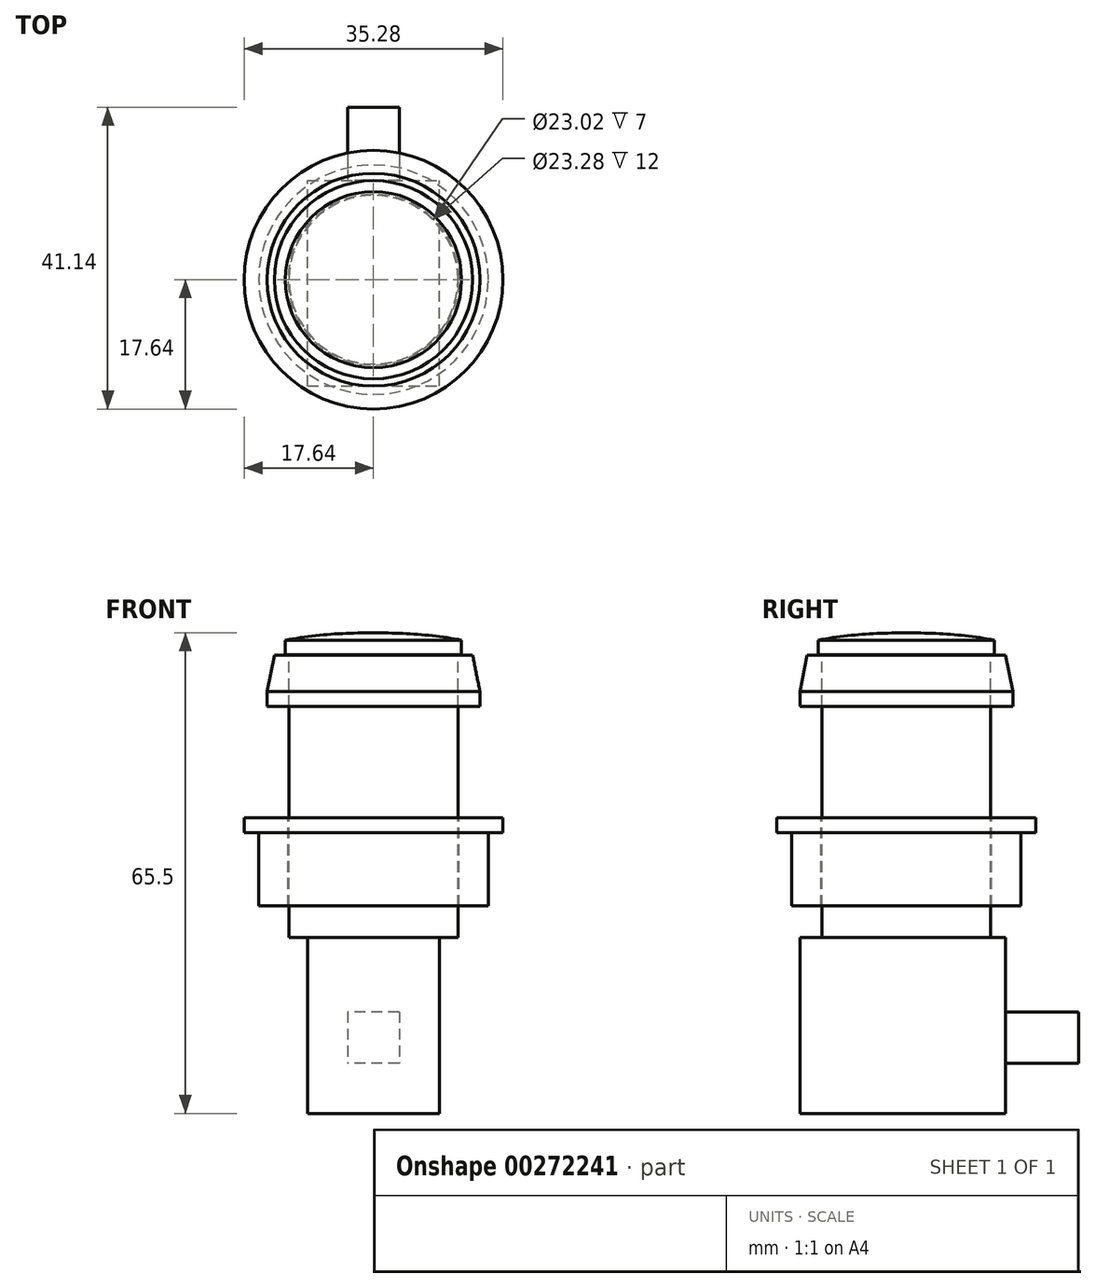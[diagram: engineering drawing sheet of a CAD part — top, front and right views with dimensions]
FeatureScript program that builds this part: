
annotation { "Feature Type Name" : "Feature", "Feature Type Description" : "" }
export const myFeature = defineFeature(function(context is Context, id is Id, definition is map)
    precondition{}
    {
        {
            var Q0;
            Q0=qCreatedBy(makeId("Front.planeOp"),FACE);
            var sketch = newSketch(context, id + "F0", { "sketchPlane" : qUnion([Q0])});
            skLineSegment(sketch, "E0.bottom", {"start": v(-11.5, 45.66) * mm, "end": v(0, 45.66) * mm});
            skLineSegment(sketch, "E0.top", {"start": v(-11.5, 7.16) * mm, "end": v(0, 7.16) * mm});
            skLineSegment(sketch, "E0.left", {"start": v(-11.5, 45.66) * mm, "end": v(-11.5, 7.16) * mm});
            skLineSegment(sketch, "E0.right", {"start": v(0, 45.66) * mm, "end": v(0, 7.16) * mm});
            skSolve(sketch);
        }
        {
            var Q0;
            Q0=makeQuery(id+"F0.imprint","IMPRINT",FACE,{"disambiguationData":[TD([[makeQuery(id+"F0.imprint","IMPRINT",EDGE,{"derivedFrom":sQuery(id+"F0.wireOp",EDGE,"E0.bottom")}),-1.0]])]});
            var Q1;
            Q1=sQuery(id+"F0.wireOp",EDGE,"E0.right");
            revolve(context, id + "F1", {"entities" : qUnion([Q0]), "axis" : qUnion([Q1]), "revolveType" : RevolveType.FULL});
        }
        {
            var Q0;
            Q0=qCreatedBy(makeId("Front.planeOp"),FACE);
            var sketch = newSketch(context, id + "F2", { "sketchPlane" : qUnion([Q0])});
            skLineSegment(sketch, "E1", {"start": v(11.5, 45.64) * mm, "end": v(11.5, 38.64) * mm});
            skLineSegment(sketch, "E2", {"start": v(11.5, 38.64) * mm, "end": v(14.5, 38.64) * mm});
            skLineSegment(sketch, "E3", {"start": v(14.5, 38.64) * mm, "end": v(14.5, 40.64) * mm});
            skLineSegment(sketch, "E4", {"start": v(11.5, 45.64) * mm, "end": v(13.5, 45.64) * mm});
            skLineSegment(sketch, "E5", {"start": v(13.5, 45.64) * mm, "end": v(14.5, 40.64) * mm});
            skLineSegment(sketch, "E6", {"start": v(0, 45.83) * mm, "end": v(0, 37.42) * mm});
            skSolve(sketch);
        }
        {
            var Q0;
            Q0=makeQuery(id+"F2.imprint","IMPRINT",FACE,{"disambiguationData":[TD([[makeQuery(id+"F2.imprint","IMPRINT",EDGE,{"derivedFrom":sQuery(id+"F2.wireOp",EDGE,"E1")}),1.0]])]});
            var Q1;
            Q1=sQuery(id+"F2.wireOp",EDGE,"E6");
            revolve(context, id + "F3", {"entities" : qUnion([Q0]), "axis" : qUnion([Q1]), "revolveType" : RevolveType.FULL});
        }
        {
            var Q0;
            Q0=qCreatedBy(makeId("Front.planeOp"),FACE);
            var sketch = newSketch(context, id + "F4", { "sketchPlane" : qUnion([Q0])});
            skLineSegment(sketch, "E7", {"start": v(0, 45.66) * mm, "end": v(-12, 45.66) * mm});
            skLineSegment(sketch, "E8", {"start": v(-12, 45.66) * mm, "end": v(-12, 47.66) * mm});
            skFitSpline(sketch, "E9", {"points": [v(-12, 47.66) * mm, v(0, 48.66) * mm], "startDerivative": vector(11.93, 2.33) * mm, "endDerivative": vector(12.44, -0.06) * mm});
            skLineSegment(sketch, "E10", {"start": v(0, 48.66) * mm, "end": v(0, 45.66) * mm});
            skSolve(sketch);
        }
        {
            var Q0;
            Q0=makeQuery(id+"F4.imprint","IMPRINT",FACE,{"disambiguationData":[TD([[makeQuery(id+"F4.imprint","IMPRINT",EDGE,{"derivedFrom":sQuery(id+"F4.wireOp",EDGE,"E7")}),-1.0]])]});
            var Q1;
            Q1=sQuery(id+"F4.wireOp",EDGE,"E10");
            revolve(context, id + "F5", {"entities" : qUnion([Q0]), "axis" : qUnion([Q1]), "revolveType" : RevolveType.FULL});
        }
        {
            var Q0;
            Q0=qCreatedBy(makeId("Front.planeOp"),FACE);
            var sketch = newSketch(context, id + "F6", { "sketchPlane" : qUnion([Q0])});
            skLineSegment(sketch, "E11.bottom", {"start": v(-9, 7.16) * mm, "end": v(9, 7.16) * mm});
            skLineSegment(sketch, "E11.top", {"start": v(-9, -16.84) * mm, "end": v(9, -16.84) * mm});
            skLineSegment(sketch, "E11.left", {"start": v(-9, 7.16) * mm, "end": v(-9, -16.84) * mm});
            skLineSegment(sketch, "E11.right", {"start": v(9, 7.16) * mm, "end": v(9, -16.84) * mm});
            skSolve(sketch);
        }
        {
            var Q0;
            Q0=makeQuery(id+"F6.imprint","IMPRINT",FACE,{"disambiguationData":[TD([[makeQuery(id+"F6.imprint","IMPRINT",EDGE,{"derivedFrom":sQuery(id+"F6.wireOp",EDGE,"E11.bottom")}),-1.0]])]});
            extrude(context, id + "F7", {"entities" : qUnion([Q0]), "depth" : 28 * mm});
        }
        {
            var Q0;
            Q0=makeQuery(id+"F7.opExtrude","SWEPT_BODY",BODY,{"disambiguationData":[OSD([sQuery(id+"F6.wireOp",EDGE,"E11.bottom"),sQuery(id+"F6.wireOp",EDGE,"E11.top"),sQuery(id+"F6.wireOp",EDGE,"E11.left"),sQuery(id+"F6.wireOp",EDGE,"E11.right")])]});
            transform(context, id + "F8", {"entities" : qUnion([Q0]), "transformType" : TransformType.TRANSLATION_3D, "dx" : 0 * mm, "dy" : 13.5 * mm, "dz" : 0 * mm, "makeCopy" : false});
        }
        {
            var Q0;
            Q0=makeQuery(id+"F7.opExtrude","CAP_FACE",FACE,{"disambiguationData":[OSD([sQuery(id+"F6.wireOp",EDGE,"E11.bottom"),sQuery(id+"F6.wireOp",EDGE,"E11.top"),sQuery(id+"F6.wireOp",EDGE,"E11.left"),sQuery(id+"F6.wireOp",EDGE,"E11.right")])],"isStart":true});
            var sketch = newSketch(context, id + "F9", { "sketchPlane" : qUnion([Q0])});
            skLineSegment(sketch, "E12.bottom", {"start": v(-3.5, -3) * mm, "end": v(3.5, -3) * mm});
            skLineSegment(sketch, "E12.top", {"start": v(-3.5, -10) * mm, "end": v(3.5, -10) * mm});
            skLineSegment(sketch, "E12.left", {"start": v(-3.5, -3) * mm, "end": v(-3.5, -10) * mm});
            skLineSegment(sketch, "E12.right", {"start": v(3.5, -3) * mm, "end": v(3.5, -10) * mm});
            skSolve(sketch);
        }
        {
            var Q0;
            Q0=makeQuery(id+"F9.imprint","IMPRINT",FACE,{"disambiguationData":[TD([[makeQuery(id+"F9.imprint","IMPRINT",EDGE,{"derivedFrom":sQuery(id+"F9.wireOp",EDGE,"E12.bottom")}),-1.0]])]});
            extrude(context, id + "F10", {"entities" : qUnion([Q0]), "operationType" : NewBodyOperationType.ADD, "depth" : 10 * mm});
        }
        {
            var Q0;
            Q0=qCreatedBy(makeId("Right.planeOp"),FACE);
            var sketch = newSketch(context, id + "F11", { "sketchPlane" : qUnion([Q0])});
            skLineSegment(sketch, "E13", {"start": v(11.64, 23.43) * mm, "end": v(11.64, 11.43) * mm});
            skLineSegment(sketch, "E14", {"start": v(11.64, 11.43) * mm, "end": v(15.64, 11.43) * mm});
            skLineSegment(sketch, "E15", {"start": v(15.64, 11.43) * mm, "end": v(15.64, 21.43) * mm});
            skLineSegment(sketch, "E16", {"start": v(15.64, 21.43) * mm, "end": v(17.64, 21.43) * mm});
            skLineSegment(sketch, "E17", {"start": v(17.64, 21.43) * mm, "end": v(17.64, 23.43) * mm});
            skLineSegment(sketch, "E18", {"start": v(17.64, 23.43) * mm, "end": v(11.64, 23.43) * mm});
            skLineSegment(sketch, "E19", {"start": v(0, 23.43) * mm, "end": v(0, 21.07) * mm});
            skLineSegment(sketch, "E20", {"start": v(11.49, 38.43) * mm, "end": v(11.64, 23.43) * mm});
            skSolve(sketch);
        }
        {
            var Q0;
            Q0=makeQuery(id+"F11.imprint","IMPRINT",FACE,{"disambiguationData":[TD([[makeQuery(id+"F11.imprint","IMPRINT",EDGE,{"derivedFrom":sQuery(id+"F11.wireOp",EDGE,"E13")}),1.0]])]});
            var Q1;
            Q1=sQuery(id+"F11.wireOp",EDGE,"E19");
            revolve(context, id + "F12", {"entities" : qUnion([Q0]), "axis" : qUnion([Q1]), "revolveType" : RevolveType.FULL});
        }
    });
